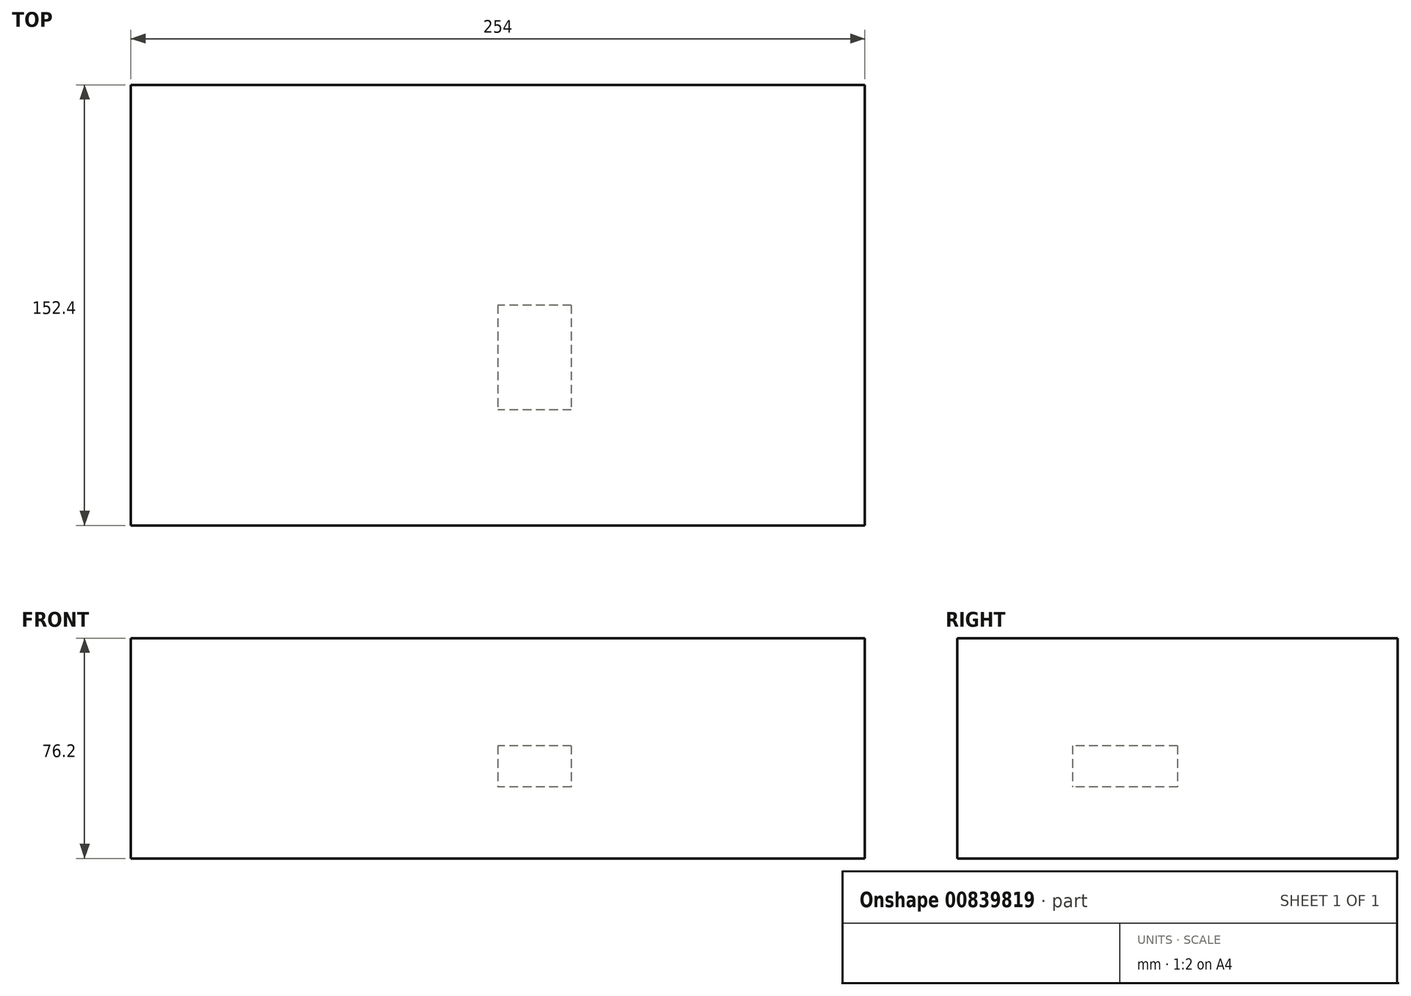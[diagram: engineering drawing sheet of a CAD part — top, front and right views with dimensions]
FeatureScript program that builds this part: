
annotation { "Feature Type Name" : "Feature", "Feature Type Description" : "" }
export const myFeature = defineFeature(function(context is Context, id is Id, definition is map)
    precondition{}
    {
        {
            var Q0;
            Q0=qCreatedBy(makeId("Top.planeOp"),FACE);
            var sketch = newSketch(context, id + "F0", { "sketchPlane" : qUnion([Q0])});
            skLineSegment(sketch, "E0.bottom", {"start": v(127, 76.2) * mm, "end": v(-127, 76.2) * mm});
            skLineSegment(sketch, "E0.top", {"start": v(127, -76.2) * mm, "end": v(-127, -76.2) * mm});
            skLineSegment(sketch, "E0.left", {"start": v(127, 76.2) * mm, "end": v(127, -76.2) * mm});
            skLineSegment(sketch, "E0.right", {"start": v(-127, 76.2) * mm, "end": v(-127, -76.2) * mm});
            skPoint(sketch, "E0.middle", {"position": v(0, 0) * mm});
            skSolve(sketch);
        }
        {
            var Q0;
            Q0 = qSketchRegion(id + "F0", true);
            extrude(context, id + "F1", {"entities" : qUnion([Q0]), "depth" : 76.2 * mm, "offsetDistance" : 25.4 * mm});
        }
        {
            var Q0;
            Q0=qCreatedBy(makeId("Right.planeOp"),FACE);
            var sketch = newSketch(context, id + "F2", { "sketchPlane" : qUnion([Q0])});
            skLineSegment(sketch, "E1.bottom", {"start": v(0, 38.96) * mm, "end": v(-36.3, 38.96) * mm});
            skLineSegment(sketch, "E1.top", {"start": v(0, 24.67) * mm, "end": v(-36.3, 24.67) * mm});
            skLineSegment(sketch, "E1.left", {"start": v(0, 38.96) * mm, "end": v(0, 24.67) * mm});
            skLineSegment(sketch, "E1.right", {"start": v(-36.3, 38.96) * mm, "end": v(-36.3, 24.67) * mm});
            skSolve(sketch);
        }
        {
            var Q0;
            Q0 = qSketchRegion(id + "F2", true);
            extrude(context, id + "F3", {"entities" : qUnion([Q0]), "depth" : 25.4 * mm, "offsetDistance" : 25.4 * mm});
        }
        {
            var Q0;
            Q0=makeQuery(id+"F1.opExtrude","SWEPT_FACE",FACE,{"disambiguationData":[OSD([sQuery(id+"F0.wireOp",EDGE,"E0.left")])]});
            var sketch = newSketch(context, id + "F4", { "sketchPlane" : qUnion([Q0])});
            skCircle(sketch, "E2", {"center": v(27.44, 38.33) * mm, "radius": 16.17 * mm});
            skSolve(sketch);
        }
        {
            var Q0;
            Q0 = qSketchRegion(id + "F4", true);
            extrude(context, id + "F5", {"entities" : qUnion([Q0]), "operationType" : NewBodyOperationType.ADD, "oppositeDirection" : true, "depth" : 6.86 * mm, "offsetDistance" : 25.4 * mm});
        }
        {
            var Q0;
            Q0=makeQuery(id+"F1.opExtrude","SWEPT_FACE",FACE,{"disambiguationData":[OSD([sQuery(id+"F0.wireOp",EDGE,"E0.right")])]});
            var sketch = newSketch(context, id + "F6", { "sketchPlane" : qUnion([Q0])});
            skLineSegment(sketch, "E3.bottom", {"start": v(62.66, 12.84) * mm, "end": v(22.97, 12.84) * mm});
            skLineSegment(sketch, "E3.top", {"start": v(62.66, 29.5) * mm, "end": v(22.97, 29.5) * mm});
            skLineSegment(sketch, "E3.left", {"start": v(62.66, 12.84) * mm, "end": v(62.66, 29.5) * mm});
            skLineSegment(sketch, "E3.right", {"start": v(22.97, 12.84) * mm, "end": v(22.97, 29.5) * mm});
            skSolve(sketch);
        }
        {
            var Q0;
            Q0 = qSketchRegion(id + "F6", true);
            extrude(context, id + "F7", {"entities" : qUnion([Q0]), "operationType" : NewBodyOperationType.ADD, "oppositeDirection" : true, "depth" : 23.37 * mm, "offsetDistance" : 25.4 * mm});
        }
    });
